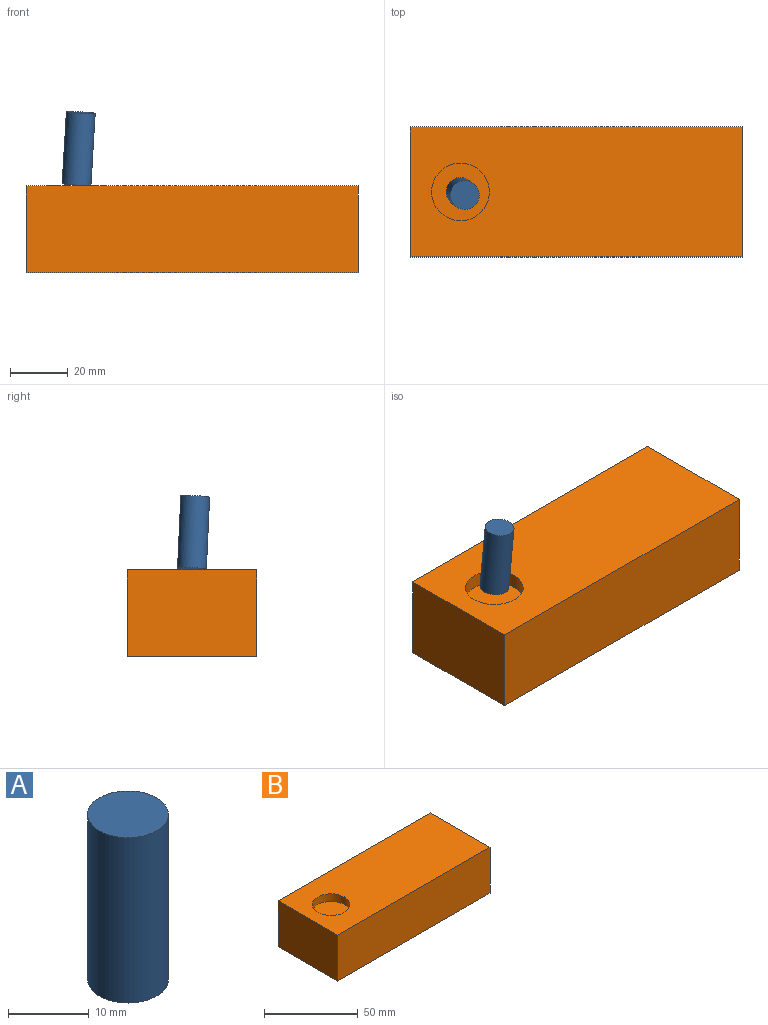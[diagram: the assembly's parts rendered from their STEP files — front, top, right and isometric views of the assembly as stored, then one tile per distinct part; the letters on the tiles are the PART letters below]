
ASSEMBLY  parts=2 mates=1
PART A: 3 faces, bbox 10x10x25 mm
  f0: cylinder r=5mm len=25mm, axis (0,0,-1), area 785.4mm2, adj f1,f2
  f1: plane 10x10mm, normal (0,0,1), area 78.5mm2, adj f0
  f2: plane 10x10mm, normal (0,0,-1), area 78.5mm2, adj f0
PART B: 8 faces, bbox 115x45x30 mm
  f0: plane 45x30mm, normal (-1,0,0), area 1350mm2, adj f1,f3,f4,f5
  f1: plane 115x30mm, normal (0,-1,0), area 3450mm2, adj f0,f2,f4,f5
  f2: plane 45x30mm, normal (1,0,0), area 1350mm2, adj f1,f3,f4,f5
  f3: plane 115x30mm, normal (0,1,0), area 3450mm2, adj f0,f2,f4,f5
  f4: plane 115x45mm, normal (0,0,1), area 4860.8mm2, adj f0,f1,f2,f3,f6
  f5: plane 115x45mm, normal (0,0,-1), area 5175mm2, adj f0,f1,f2,f3
  f6: cylinder r=10mm len=20mm, axis (0,0,1), area 314.2mm2, adj f4,f7
  f7: plane 20x20mm, normal (0,0,1), area 314.2mm2, adj f6
PLACE A rot(axis=(0.14,-0.99,-0.03),177deg) t=(-38.52,-1.11,55.43)mm
PLACE B at identity fixed
MATE ball B.f6 <-> A.f0  axis (0,0,1) through (-40,0,30.5)mm
